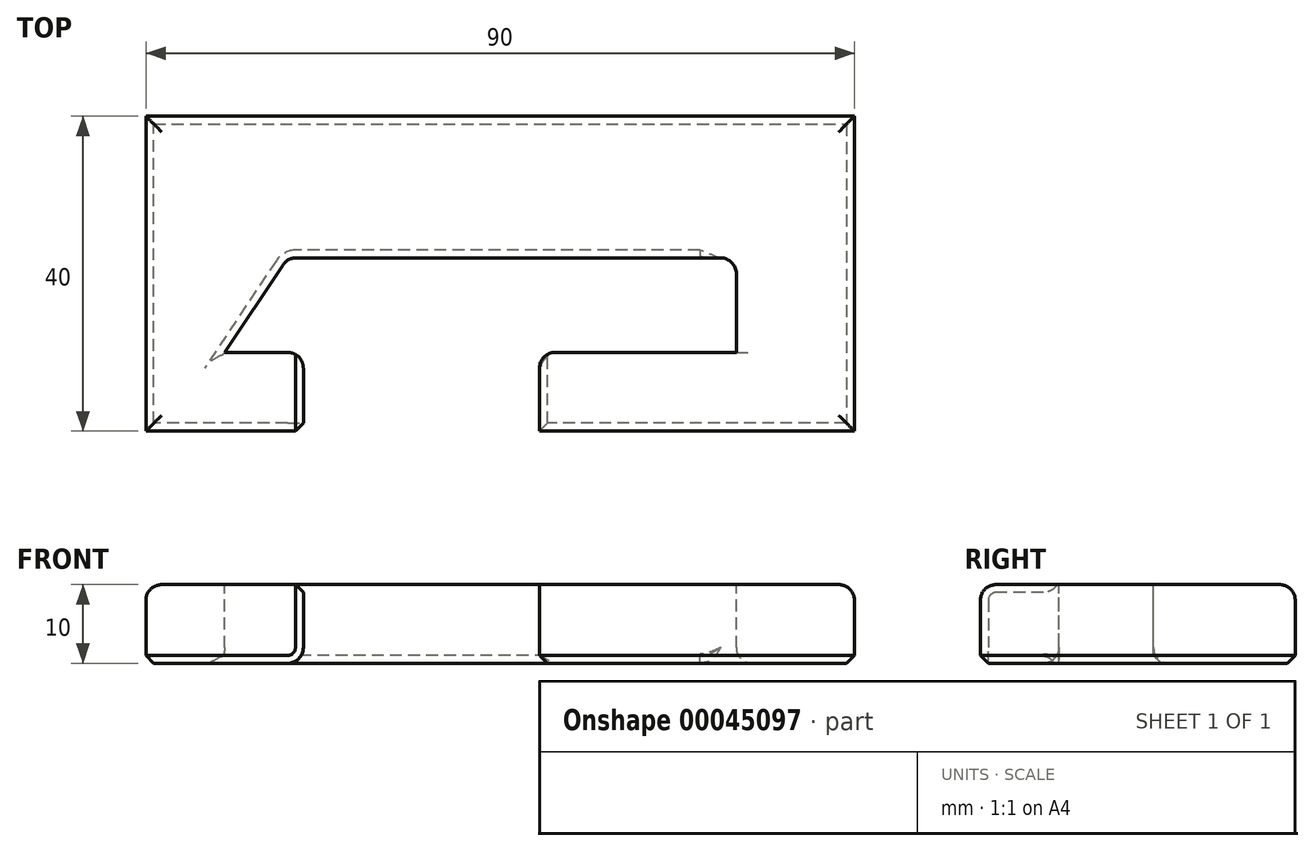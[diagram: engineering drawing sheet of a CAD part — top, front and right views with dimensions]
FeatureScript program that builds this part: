
annotation { "Feature Type Name" : "Feature", "Feature Type Description" : "" }
export const myFeature = defineFeature(function(context is Context, id is Id, definition is map)
    precondition{}
    {
        {
            var Q0;
            Q0=qCreatedBy(makeId("Top.planeOp"),FACE);
            var sketch = newSketch(context, id + "F0", { "sketchPlane" : qUnion([Q0])});
            skLineSegment(sketch, "E0.rect.bottom", {"start": v(45, 20) * mm, "end": v(-45, 20) * mm});
            skLineSegment(sketch, "E0.rect.top", {"start": v(45, -20) * mm, "end": v(-45, -20) * mm});
            skLineSegment(sketch, "E0.rect.left", {"start": v(45, 20) * mm, "end": v(45, -20) * mm});
            skLineSegment(sketch, "E0.rect.right", {"start": v(-45, 20) * mm, "end": v(-45, -20) * mm});
            skPoint(sketch, "E0.rect.middle", {"position": v(0, 0) * mm});
            skSolve(sketch);
        }
        {
            var Q0;
            Q0=makeQuery(id+"F0.imprint","IMPRINT",FACE,{"disambiguationData":[TD([[makeQuery(id+"F0.imprint","IMPRINT",EDGE,{"derivedFrom":sQuery(id+"F0.wireOp",EDGE,"E0.rect.bottom")}),1.0]])]});
            extrude(context, id + "F1", {"entities" : qUnion([Q0]), "depth" : 10 * mm});
        }
        {
            var Q0;
            Q0=makeQuery(id+"F1.opExtrude","CAP_FACE",FACE,{"disambiguationData":[OSD([sQuery(id+"F0.wireOp",EDGE,"E0.rect.bottom"),sQuery(id+"F0.wireOp",EDGE,"E0.rect.top"),sQuery(id+"F0.wireOp",EDGE,"E0.rect.left"),sQuery(id+"F0.wireOp",EDGE,"E0.rect.right")])],"isStart":false});
            var sketch = newSketch(context, id + "F2", { "sketchPlane" : qUnion([Q0])});
            skLineSegment(sketch, "E1", {"start": v(-45, -20) * mm, "end": v(-25, -20) * mm, "construction": true});
            skLineSegment(sketch, "E2.bottom", {"start": v(-25, -20) * mm, "end": v(5, -20) * mm});
            skLineSegment(sketch, "E2.top", {"start": v(-25, 2) * mm, "end": v(5, 2) * mm});
            skLineSegment(sketch, "E2.left", {"start": v(-25, -20) * mm, "end": v(-25, 2) * mm});
            skLineSegment(sketch, "E2.right", {"start": v(5, -20) * mm, "end": v(5, 2) * mm});
            skLineSegment(sketch, "E3.top", {"start": v(-25, -10) * mm, "end": v(-35, -10) * mm});
            skLineSegment(sketch, "E3.left", {"start": v(-25, 2) * mm, "end": v(-25, -10) * mm});
            skLineSegment(sketch, "E4.bottom", {"start": v(5, 2) * mm, "end": v(30, 2) * mm});
            skLineSegment(sketch, "E4.top", {"start": v(5, -10) * mm, "end": v(30, -10) * mm});
            skLineSegment(sketch, "E4.left", {"start": v(5, 2) * mm, "end": v(5, -10) * mm});
            skLineSegment(sketch, "E4.right", {"start": v(30, 2) * mm, "end": v(30, -10) * mm});
            skLineSegment(sketch, "E5", {"start": v(-25, 2) * mm, "end": v(-27, 2) * mm});
            skLineSegment(sketch, "E6", {"start": v(-27, 2) * mm, "end": v(-35, -10) * mm});
            skSolve(sketch);
        }
        {
            var Q0;
            Q0=makeQuery(id+"F2.imprint","IMPRINT",FACE,{"disambiguationData":[TD([[makeQuery(id+"F2.imprint","IMPRINT",EDGE,{"derivedFrom":sQuery(id+"F2.wireOp",EDGE,"E3.bottom")}),1.0]])]});
            var Q1;
            Q1=makeQuery(id+"F2.imprint","IMPRINT",FACE,{"disambiguationData":[TD([[makeQuery(id+"F2.imprint","IMPRINT",EDGE,{"derivedFrom":sQuery(id+"F2.wireOp",EDGE,"E2.bottom")}),-1.0]])]});
            var Q2;
            Q2=makeQuery(id+"F2.imprint","IMPRINT",FACE,{"disambiguationData":[TD([[makeQuery(id+"F2.imprint","IMPRINT",EDGE,{"derivedFrom":sQuery(id+"F2.wireOp",EDGE,"E3.top")}),-1.0]])]});
            var Q3;
            Q3=makeQuery(id+"F2.imprint","IMPRINT",FACE,{"disambiguationData":[TD([[makeQuery(id+"F2.imprint","IMPRINT",EDGE,{"derivedFrom":sQuery(id+"F2.wireOp",EDGE,"E4.bottom")}),-1.0]])]});
            extrude(context, id + "F3", {"entities" : qUnion([Q0, Q1, Q2, Q3]), "operationType" : NewBodyOperationType.REMOVE, "oppositeDirection" : true, "depth" : 25 * mm});
        }
        {
            var Q0;
            Q0=makeQuery(id+"F3.boolean.opBoolean","COPY",EDGE,{"derivedFrom":makeQuery(id+"F3.opExtrude","CAP_EDGE",EDGE,{"disambiguationData":[OSD([sQuery(id+"F2.wireOp",EDGE,"E2.top"),sQuery(id+"F2.wireOp",EDGE,"E4.bottom")])],"isStart":true})});
            var Q1;
            Q1=makeQuery(id+"F3.boolean.opBoolean","COPY",EDGE,{"derivedFrom":makeQuery(id+"F3.opExtrude","CAP_EDGE",EDGE,{"disambiguationData":[OSD([sQuery(id+"F2.wireOp",EDGE,"E2.right")])],"isStart":true})});
            var Q2;
            Q2=makeQuery(id+"F1.opExtrude","CAP_EDGE",EDGE,{"disambiguationData":[OSD([sQuery(id+"F0.wireOp",EDGE,"E0.rect.bottom")])],"isStart":false});
            var Q3;
            {var subQ0=sQuery(id+"F0.wireOp",EDGE,"E0.rect.top");var subQ1=sQuery(id+"F0.wireOp",EDGE,"E0.rect.left");Q3=makeQuery(id+"F3.boolean.opBoolean","SPLIT",EDGE,{"disambiguationData":[TD([makeQuery(id+"F1.opExtrude","SWEPT_FACE",FACE,{"disambiguationData":[OSD([subQ1])]})])],"derivedFrom":makeQuery(id+"F1.opExtrude","CAP_EDGE",EDGE,{"disambiguationData":[OSD([subQ0])],"isStart":false})});}
            var Q4;
            Q4=makeQuery(id+"F1.opExtrude","CAP_EDGE",EDGE,{"disambiguationData":[OSD([sQuery(id+"F0.wireOp",EDGE,"E0.rect.left")])],"isStart":false});
            var Q5;
            Q5=makeQuery(id+"F3.boolean.opBoolean","COPY",EDGE,{"derivedFrom":makeQuery(id+"F3.opExtrude","CAP_EDGE",EDGE,{"disambiguationData":[OSD([sQuery(id+"F2.wireOp",EDGE,"E3.top")])],"isStart":true})});
            var Q6;
            Q6=makeQuery(id+"F3.boolean.opBoolean","COPY",EDGE,{"derivedFrom":makeQuery(id+"F3.opExtrude","CAP_EDGE",EDGE,{"disambiguationData":[OSD([sQuery(id+"F2.wireOp",EDGE,"E2.left")])],"isStart":true})});
            var Q7;
            {var subQ0=sQuery(id+"F0.wireOp",EDGE,"E0.rect.top");var subQ1=sQuery(id+"F0.wireOp",EDGE,"E0.rect.right");Q7=makeQuery(id+"F3.boolean.opBoolean","SPLIT",EDGE,{"disambiguationData":[TD([makeQuery(id+"F1.opExtrude","SWEPT_FACE",FACE,{"disambiguationData":[OSD([subQ1])]})])],"derivedFrom":makeQuery(id+"F1.opExtrude","CAP_EDGE",EDGE,{"disambiguationData":[OSD([subQ0])],"isStart":false})});}
            var Q8;
            Q8=makeQuery(id+"F1.opExtrude","CAP_EDGE",EDGE,{"disambiguationData":[OSD([sQuery(id+"F0.wireOp",EDGE,"E0.rect.right")])],"isStart":false});
            var Q9;
            Q9=makeQuery(id+"F3.boolean.opBoolean","COPY",EDGE,{"derivedFrom":makeQuery(id+"F3.opExtrude","CAP_EDGE",EDGE,{"disambiguationData":[OSD([sQuery(id+"F2.wireOp",EDGE,"3d185214-d2e6-4e43-a952-977d2766035b")])],"isStart":true})});
            var Q10;
            Q10=makeQuery(id+"F3.boolean.opBoolean","INTERSECT",EDGE,{"derivedFrom":[makeQuery(id+"F1.opExtrude","CAP_FACE",FACE,{"disambiguationData":[OSD([sQuery(id+"F0.wireOp",EDGE,"E0.rect.bottom"),sQuery(id+"F0.wireOp",EDGE,"E0.rect.top"),sQuery(id+"F0.wireOp",EDGE,"E0.rect.left"),sQuery(id+"F0.wireOp",EDGE,"E0.rect.right")])],"isStart":true}),makeQuery(id+"F3.opExtrude","SWEPT_FACE",FACE,{"disambiguationData":[OSD([sQuery(id+"F2.wireOp",EDGE,"E2.left")])]})]});
            var Q11;
            Q11=makeQuery(id+"F3.boolean.opBoolean","COPY",EDGE,{"derivedFrom":makeQuery(id+"F3.opExtrude","CAP_EDGE",EDGE,{"disambiguationData":[OSD([sQuery(id+"F2.wireOp",EDGE,"E4.right")])],"isStart":true})});
            var Q12;
            Q12=makeQuery(id+"F3.boolean.opBoolean","INTERSECT",EDGE,{"derivedFrom":[makeQuery(id+"F1.opExtrude","CAP_FACE",FACE,{"disambiguationData":[OSD([sQuery(id+"F0.wireOp",EDGE,"E0.rect.bottom"),sQuery(id+"F0.wireOp",EDGE,"E0.rect.top"),sQuery(id+"F0.wireOp",EDGE,"E0.rect.left"),sQuery(id+"F0.wireOp",EDGE,"E0.rect.right")])],"isStart":true}),makeQuery(id+"F3.opExtrude","SWEPT_FACE",FACE,{"disambiguationData":[OSD([sQuery(id+"F2.wireOp",EDGE,"E4.right")])]})]});
            var Q13;
            Q13=makeQuery(id+"F3.boolean.opBoolean","COPY",EDGE,{"derivedFrom":makeQuery(id+"F3.opExtrude","SWEPT_EDGE",EDGE,{"disambiguationData":[OSD([sQuery(id+"F2.wireOp",EDGE,"E4.bottom"),sQuery(id+"F2.wireOp",EDGE,"E4.right")])]})});
            var Q14;
            Q14=makeQuery(id+"F3.boolean.opBoolean","COPY",EDGE,{"derivedFrom":makeQuery(id+"F3.opExtrude","CAP_EDGE",EDGE,{"disambiguationData":[OSD([sQuery(id+"F2.wireOp",EDGE,"E6")])],"isStart":true})});
            var Q15;
            Q15=makeQuery(id+"F3.boolean.opBoolean","COPY",EDGE,{"derivedFrom":makeQuery(id+"F3.opExtrude","SWEPT_EDGE",EDGE,{"disambiguationData":[OSD([sQuery(id+"F2.wireOp",EDGE,"E5"),sQuery(id+"F2.wireOp",EDGE,"E6")])]})});
            fillet(context, id + "F4", {"entities" : qUnion([Q0, Q1, Q2, Q3, Q4, Q5, Q6, Q7, Q8, Q9, Q10, Q11, Q12, Q13, Q14, Q15]), "radius" : 2 * mm, "tangentPropagation" : true, "allowEdgeOverflow" : false});
        }
        {
            var Q0;
            Q0=makeQuery(id+"F1.opExtrude","CAP_EDGE",EDGE,{"disambiguationData":[OSD([sQuery(id+"F0.wireOp",EDGE,"E0.rect.right")])],"isStart":true});
            var Q1;
            {var subQ0=sQuery(id+"F0.wireOp",EDGE,"E0.rect.top");var subQ1=sQuery(id+"F0.wireOp",EDGE,"E0.rect.right");Q1=makeQuery(id+"F3.boolean.opBoolean","SPLIT",EDGE,{"disambiguationData":[TD([makeQuery(id+"F1.opExtrude","SWEPT_FACE",FACE,{"disambiguationData":[OSD([subQ1])]})])],"derivedFrom":makeQuery(id+"F1.opExtrude","CAP_EDGE",EDGE,{"disambiguationData":[OSD([subQ0])],"isStart":true})});}
            var Q2;
            Q2=makeQuery(id+"F1.opExtrude","CAP_EDGE",EDGE,{"disambiguationData":[OSD([sQuery(id+"F0.wireOp",EDGE,"E0.rect.bottom")])],"isStart":true});
            var Q3;
            Q3=makeQuery(id+"F3.boolean.opBoolean","INTERSECT",EDGE,{"derivedFrom":[makeQuery(id+"F1.opExtrude","CAP_FACE",FACE,{"disambiguationData":[OSD([sQuery(id+"F0.wireOp",EDGE,"E0.rect.bottom"),sQuery(id+"F0.wireOp",EDGE,"E0.rect.top"),sQuery(id+"F0.wireOp",EDGE,"E0.rect.left"),sQuery(id+"F0.wireOp",EDGE,"E0.rect.right")])],"isStart":true}),makeQuery(id+"F3.opExtrude","SWEPT_FACE",FACE,{"disambiguationData":[OSD([sQuery(id+"F2.wireOp",EDGE,"3d185214-d2e6-4e43-a952-977d2766035b")])]})]});
            var Q4;
            Q4=makeQuery(id+"F3.boolean.opBoolean","INTERSECT",EDGE,{"derivedFrom":[makeQuery(id+"F1.opExtrude","CAP_FACE",FACE,{"disambiguationData":[OSD([sQuery(id+"F0.wireOp",EDGE,"E0.rect.bottom"),sQuery(id+"F0.wireOp",EDGE,"E0.rect.top"),sQuery(id+"F0.wireOp",EDGE,"E0.rect.left"),sQuery(id+"F0.wireOp",EDGE,"E0.rect.right")])],"isStart":true}),makeQuery(id+"F3.opExtrude","SWEPT_FACE",FACE,{"disambiguationData":[OSD([sQuery(id+"F2.wireOp",EDGE,"E2.top")])]})]});
            var Q5;
            Q5=makeQuery(id+"F3.boolean.opBoolean","INTERSECT",EDGE,{"derivedFrom":[makeQuery(id+"F1.opExtrude","CAP_FACE",FACE,{"disambiguationData":[OSD([sQuery(id+"F0.wireOp",EDGE,"E0.rect.bottom"),sQuery(id+"F0.wireOp",EDGE,"E0.rect.top"),sQuery(id+"F0.wireOp",EDGE,"E0.rect.left"),sQuery(id+"F0.wireOp",EDGE,"E0.rect.right")])],"isStart":true}),makeQuery(id+"F3.opExtrude","SWEPT_FACE",FACE,{"disambiguationData":[OSD([sQuery(id+"F2.wireOp",EDGE,"E2.right")])]})]});
            var Q6;
            {var subQ0=sQuery(id+"F0.wireOp",EDGE,"E0.rect.top");var subQ1=sQuery(id+"F0.wireOp",EDGE,"E0.rect.left");Q6=makeQuery(id+"F3.boolean.opBoolean","SPLIT",EDGE,{"disambiguationData":[TD([makeQuery(id+"F1.opExtrude","SWEPT_FACE",FACE,{"disambiguationData":[OSD([subQ1])]})])],"derivedFrom":makeQuery(id+"F1.opExtrude","CAP_EDGE",EDGE,{"disambiguationData":[OSD([subQ0])],"isStart":true})});}
            var Q7;
            Q7=makeQuery(id+"F1.opExtrude","CAP_EDGE",EDGE,{"disambiguationData":[OSD([sQuery(id+"F0.wireOp",EDGE,"E0.rect.left")])],"isStart":true});
            chamfer(context, id + "F5", {"entities" : qUnion([Q0, Q1, Q2, Q3, Q4, Q5, Q6, Q7]), "width" : 1 * mm, "tangentPropagation" : true});
        }
        {
            var Q0;
            Q0=makeQuery(id+"F3.boolean.opBoolean","COPY",EDGE,{"derivedFrom":makeQuery(id+"F3.opExtrude","SWEPT_EDGE",EDGE,{"disambiguationData":[OSD([sQuery(id+"F2.wireOp",EDGE,"E2.left"),sQuery(id+"F2.wireOp",EDGE,"E3.top"),sQuery(id+"F2.wireOp",EDGE,"E3.left")])]})});
            var Q1;
            Q1=makeQuery(id+"F3.boolean.opBoolean","COPY",EDGE,{"derivedFrom":makeQuery(id+"F3.opExtrude","SWEPT_EDGE",EDGE,{"disambiguationData":[OSD([sQuery(id+"F0.wireOp",EDGE,"E0.rect.top"),sQuery(id+"F2.wireOp",EDGE,"E2.bottom"),sQuery(id+"F2.wireOp",EDGE,"E2.right")])]})});
            var Q2;
            Q2=makeQuery(id+"F3.boolean.opBoolean","COPY",EDGE,{"derivedFrom":makeQuery(id+"F3.opExtrude","SWEPT_EDGE",EDGE,{"disambiguationData":[OSD([sQuery(id+"F2.wireOp",EDGE,"E2.top"),sQuery(id+"F2.wireOp",EDGE,"E2.right")])]})});
            var Q3;
            Q3=makeQuery(id+"F3.boolean.opBoolean","COPY",EDGE,{"derivedFrom":makeQuery(id+"F3.opExtrude","SWEPT_EDGE",EDGE,{"disambiguationData":[OSD([sQuery(id+"F2.wireOp",EDGE,"E2.top"),sQuery(id+"F2.wireOp",EDGE,"E3.left"),sQuery(id+"F2.wireOp",EDGE,"3d185214-d2e6-4e43-a952-977d2766035b")])]})});
            fillet(context, id + "F6", {"entities" : qUnion([Q0, Q1, Q2, Q3]), "radius" : 2 * mm, "tangentPropagation" : true, "allowEdgeOverflow" : false});
        }
        {
            var Q0;
            {var subQ0=makeQuery(id+"F3.opExtrude","SWEPT_FACE",FACE,{"disambiguationData":[OSD([sQuery(id+"F2.wireOp",EDGE,"E2.top")])]});Q0=makeQuery(id+"F5.opChamfer","BLEND_EDGE",EDGE,{"blendedFrom":[makeQuery(id+"F3.boolean.opBoolean","INTERSECT",EDGE,{"derivedFrom":[makeQuery(id+"F1.opExtrude","CAP_FACE",FACE,{"disambiguationData":[OSD([sQuery(id+"F0.wireOp",EDGE,"E0.rect.bottom"),sQuery(id+"F0.wireOp",EDGE,"E0.rect.top"),sQuery(id+"F0.wireOp",EDGE,"E0.rect.left"),sQuery(id+"F0.wireOp",EDGE,"E0.rect.right")])],"isStart":true}),subQ0]}),makeQuery(id+"F3.boolean.opBoolean","COPY",FACE,{"derivedFrom":subQ0})],"blendedInto":[makeQuery(id+"F3.boolean.opBoolean","COPY",FACE,{"derivedFrom":subQ0})]});}
            var Q1;
            {var subQ0=makeQuery(id+"F3.opExtrude","SWEPT_FACE",FACE,{"disambiguationData":[OSD([sQuery(id+"F2.wireOp",EDGE,"E2.right")])]});Q1=makeQuery(id+"F5.opChamfer","BLEND_EDGE",EDGE,{"blendedFrom":[makeQuery(id+"F3.boolean.opBoolean","INTERSECT",EDGE,{"derivedFrom":[makeQuery(id+"F1.opExtrude","CAP_FACE",FACE,{"disambiguationData":[OSD([sQuery(id+"F0.wireOp",EDGE,"E0.rect.bottom"),sQuery(id+"F0.wireOp",EDGE,"E0.rect.top"),sQuery(id+"F0.wireOp",EDGE,"E0.rect.left"),sQuery(id+"F0.wireOp",EDGE,"E0.rect.right")])],"isStart":true}),subQ0]}),makeQuery(id+"F3.boolean.opBoolean","COPY",FACE,{"derivedFrom":subQ0})],"blendedInto":[makeQuery(id+"F3.boolean.opBoolean","COPY",FACE,{"derivedFrom":subQ0})]});}
            var Q2;
            {var subQ0=sQuery(id+"F2.wireOp",EDGE,"E2.top");Q2=makeQuery(id+"F6.opFillet","BLEND_EDGE",EDGE,{"blendedFrom":[makeQuery(id+"F3.boolean.opBoolean","COPY",EDGE,{"derivedFrom":makeQuery(id+"F3.opExtrude","SWEPT_EDGE",EDGE,{"disambiguationData":[OSD([subQ0,sQuery(id+"F2.wireOp",EDGE,"E2.right")])]})}),makeQuery(id+"F5.opChamfer","BLEND_FACE",FACE,{"disambiguationData":[OSD([sQuery(id+"F0.wireOp",EDGE,"E0.rect.bottom"),sQuery(id+"F0.wireOp",EDGE,"E0.rect.top"),sQuery(id+"F0.wireOp",EDGE,"E0.rect.left"),sQuery(id+"F0.wireOp",EDGE,"E0.rect.right"),subQ0])]})],"blendedInto":[makeQuery(id+"F5.opChamfer","BLEND_FACE",FACE,{"disambiguationData":[OSD([sQuery(id+"F0.wireOp",EDGE,"E0.rect.bottom"),sQuery(id+"F0.wireOp",EDGE,"E0.rect.top"),sQuery(id+"F0.wireOp",EDGE,"E0.rect.left"),sQuery(id+"F0.wireOp",EDGE,"E0.rect.right"),subQ0])]})]});}
            var Q3;
            {var subQ0=sQuery(id+"F2.wireOp",EDGE,"E2.right");Q3=makeQuery(id+"F6.opFillet","BLEND_EDGE",EDGE,{"blendedFrom":[makeQuery(id+"F3.boolean.opBoolean","COPY",EDGE,{"derivedFrom":makeQuery(id+"F3.opExtrude","SWEPT_EDGE",EDGE,{"disambiguationData":[OSD([sQuery(id+"F2.wireOp",EDGE,"E2.top"),subQ0])]})}),makeQuery(id+"F5.opChamfer","BLEND_FACE",FACE,{"disambiguationData":[OSD([sQuery(id+"F0.wireOp",EDGE,"E0.rect.bottom"),sQuery(id+"F0.wireOp",EDGE,"E0.rect.top"),sQuery(id+"F0.wireOp",EDGE,"E0.rect.left"),sQuery(id+"F0.wireOp",EDGE,"E0.rect.right"),subQ0])]})],"blendedInto":[makeQuery(id+"F5.opChamfer","BLEND_FACE",FACE,{"disambiguationData":[OSD([sQuery(id+"F0.wireOp",EDGE,"E0.rect.bottom"),sQuery(id+"F0.wireOp",EDGE,"E0.rect.top"),sQuery(id+"F0.wireOp",EDGE,"E0.rect.left"),sQuery(id+"F0.wireOp",EDGE,"E0.rect.right"),subQ0])]})]});}
            var Q4;
            {var subQ0=sQuery(id+"F2.wireOp",EDGE,"E2.top");Q4=makeQuery(id+"F6.opFillet","BLEND_EDGE",EDGE,{"blendedFrom":[makeQuery(id+"F3.boolean.opBoolean","COPY",EDGE,{"derivedFrom":makeQuery(id+"F3.opExtrude","SWEPT_EDGE",EDGE,{"disambiguationData":[OSD([subQ0,sQuery(id+"F2.wireOp",EDGE,"E3.left"),sQuery(id+"F2.wireOp",EDGE,"3d185214-d2e6-4e43-a952-977d2766035b")])]})}),makeQuery(id+"F5.opChamfer","BLEND_FACE",FACE,{"disambiguationData":[OSD([sQuery(id+"F0.wireOp",EDGE,"E0.rect.bottom"),sQuery(id+"F0.wireOp",EDGE,"E0.rect.top"),sQuery(id+"F0.wireOp",EDGE,"E0.rect.left"),sQuery(id+"F0.wireOp",EDGE,"E0.rect.right"),subQ0])]})],"blendedInto":[makeQuery(id+"F5.opChamfer","BLEND_FACE",FACE,{"disambiguationData":[OSD([sQuery(id+"F0.wireOp",EDGE,"E0.rect.bottom"),sQuery(id+"F0.wireOp",EDGE,"E0.rect.top"),sQuery(id+"F0.wireOp",EDGE,"E0.rect.left"),sQuery(id+"F0.wireOp",EDGE,"E0.rect.right"),subQ0])]})]});}
            var Q5;
            {var subQ0=makeQuery(id+"F3.opExtrude","SWEPT_FACE",FACE,{"disambiguationData":[OSD([sQuery(id+"F2.wireOp",EDGE,"3d185214-d2e6-4e43-a952-977d2766035b")])]});Q5=makeQuery(id+"F5.opChamfer","BLEND_EDGE",EDGE,{"blendedFrom":[makeQuery(id+"F3.boolean.opBoolean","INTERSECT",EDGE,{"derivedFrom":[makeQuery(id+"F1.opExtrude","CAP_FACE",FACE,{"disambiguationData":[OSD([sQuery(id+"F0.wireOp",EDGE,"E0.rect.bottom"),sQuery(id+"F0.wireOp",EDGE,"E0.rect.top"),sQuery(id+"F0.wireOp",EDGE,"E0.rect.left"),sQuery(id+"F0.wireOp",EDGE,"E0.rect.right")])],"isStart":true}),subQ0]}),makeQuery(id+"F3.boolean.opBoolean","COPY",FACE,{"derivedFrom":subQ0})],"blendedInto":[makeQuery(id+"F3.boolean.opBoolean","COPY",FACE,{"derivedFrom":subQ0})]});}
            fillet(context, id + "F7", {"entities" : qUnion([Q0, Q1, Q2, Q3, Q4, Q5]), "radius" : 0.5 * mm, "tangentPropagation" : true, "allowEdgeOverflow" : false});
        }
    });
